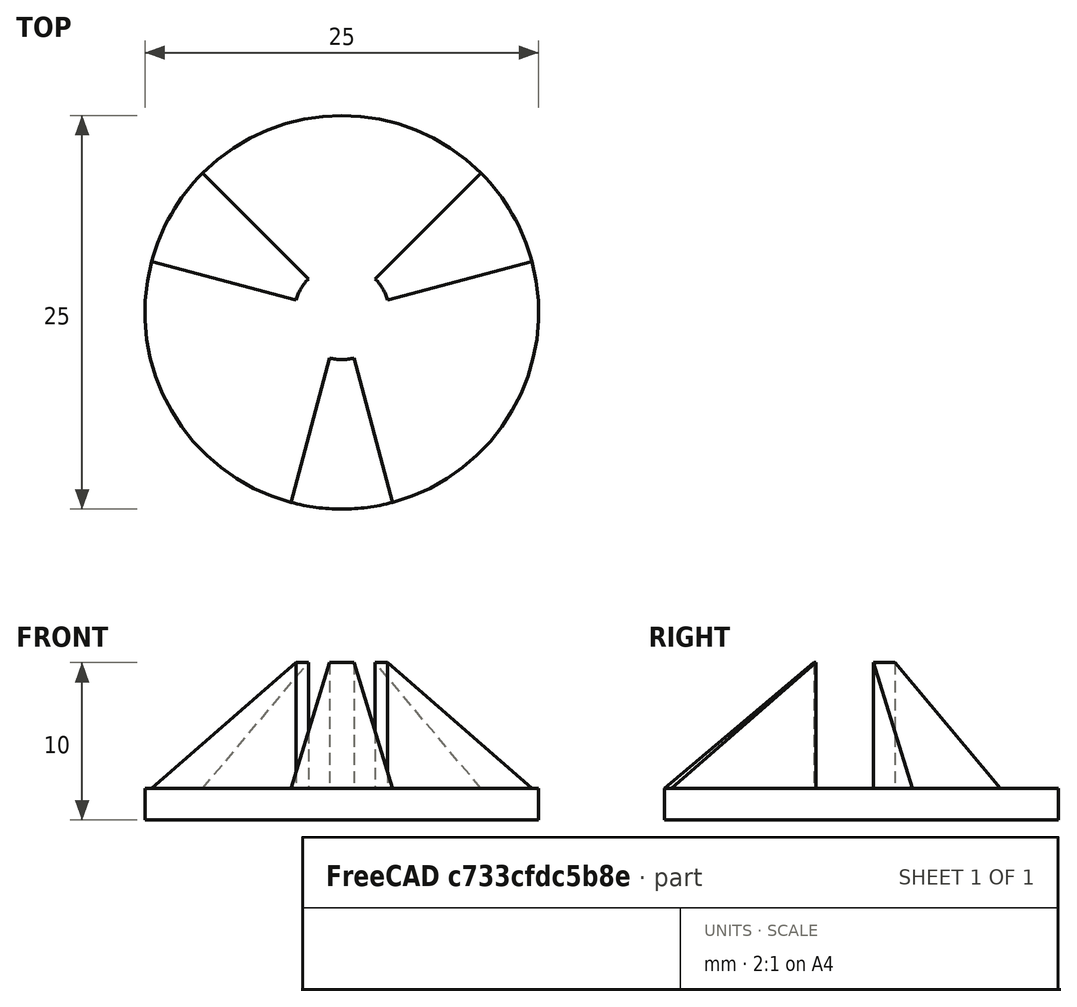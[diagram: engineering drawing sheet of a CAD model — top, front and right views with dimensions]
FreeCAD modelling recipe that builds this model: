
FCSTD DOCUMENT  (FreeCAD 0.19R24291 (Git))
Label: цнетратор 0
License: All rights reserved
LicenseURL: http://en.wikipedia.org/wiki/All_rights_reserved
objects: Sketcher::SketchObject×2, PartDesign::Revolution×2, Mesh::Feature×1, PartDesign::PolarPattern×1, PartDesign::Body×1
note: 8 computed .brp shape members not serialized (recipe doc carries the construction recipe); baked Part::Feature solids carry a one-line shape summary decoded from their .brp

FEATURE [Mesh::Feature] piramide
FEATURE [Sketcher::SketchObject] Sketch
  FullyConstrained = true
  MapMode = 5
  Placement = pos=(0,0,0) rot=(0.57735,0.57735,0.57735;2.0944rad)
  Support = -> [YZ_Plane]
  sketch-geometry (5):
    g0: LineSegment StartX=-12.5 StartY=0 StartZ=0 EndX=-3 EndY=8 EndZ=0
    g1: LineSegment StartX=-12.5 StartY=0 StartZ=0 EndX=-12.5 EndY=-2 EndZ=0
    g2: LineSegment StartX=-12.5 StartY=-2 StartZ=0 EndX=0 EndY=-2 EndZ=0
    g3: LineSegment StartX=0 StartY=-2 StartZ=0 EndX=0 EndY=0 EndZ=0
    g4: LineSegment StartX=0 StartY=0 StartZ=0 EndX=-12.5 EndY=0 EndZ=0
  constraints (14):
    c: Distance(g0,g-1) = 8
    c: PointOnObject(g0,g-1)
    c: Distance(g-1,g0) = 12.5
    c: Distance(g0,g-2) = 3
    c: Coincident(g1,g0)
    c: Vertical(g1)
    c: Coincident(g2,g1)
    c: PointOnObject(g2,g-2)
    c: Horizontal(g2)
    c: Coincident(g3,g2)
    c: Coincident(g3,g-1)
    c: Coincident(g4,g3)
    c: Coincident(g4,g1)
    c: Distance(g3) = 2
FEATURE [PartDesign::Revolution] Revolution
  Angle = 360
  Axis = (-2e-16,3e-16,1)
  Base = (0,0,0)
  Placement = pos=(0,0,0) rot=(0.57735,0.57735,0.57735;2.0944rad)
  Profile = -> Sketch
  ReferenceAxis = -> Sketch [V_Axis]
FEATURE [Sketcher::SketchObject] Sketch001
  FullyConstrained = true
  MapMode = 5
  Placement = pos=(0,0,0) rot=(0.57735,0.57735,0.57735;2.0944rad)
  Support = -> [YZ_Plane]
  sketch-geometry (3):
    g0: LineSegment StartX=-12.5 StartY=0 StartZ=0 EndX=-3 EndY=8 EndZ=0
    g1: LineSegment StartX=-3 StartY=8 StartZ=0 EndX=-3 EndY=0 EndZ=0
    g2: LineSegment StartX=-3 StartY=0 StartZ=0 EndX=-12.5 EndY=0 EndZ=0
  constraints (9):
    c: PointOnObject(g0,g-1)
    c: Coincident(g1,g0)
    c: PointOnObject(g1,g-1)
    c: Vertical(g1)
    c: Coincident(g2,g1)
    c: Coincident(g2,g0)
    c: Distance(g1) = 8
    c: Distance(g0,g-2) = 12.5
    c: Distance(g1,g-2) = 3
FEATURE [PartDesign::Revolution] Revolution001
  Angle = 30
  Axis = (-2e-16,3e-16,1)
  Base = (0,0,0)
  BaseFeature = -> Revolution
  Midplane = true
  Placement = pos=(0,0,0) rot=(0.57735,0.57735,0.57735;2.0944rad)
  Profile = -> Sketch001
  ReferenceAxis = -> Sketch001 [V_Axis]
FEATURE [PartDesign::PolarPattern] PolarPattern
  Angle = 360
  Axis = -> Sketch001 [V_Axis]
  BaseFeature = -> Revolution001
  Occurrences = 3
  Originals = -> [Revolution001]
  Placement = pos=(0,0,0) rot=(0.57735,0.57735,0.57735;2.0944rad)
FEATURE [PartDesign::Body] Body
  Group = -> [Sketch,Revolution,Sketch001,Revolution001,PolarPattern]
  Origin = -> Origin
  Tip = -> PolarPattern
